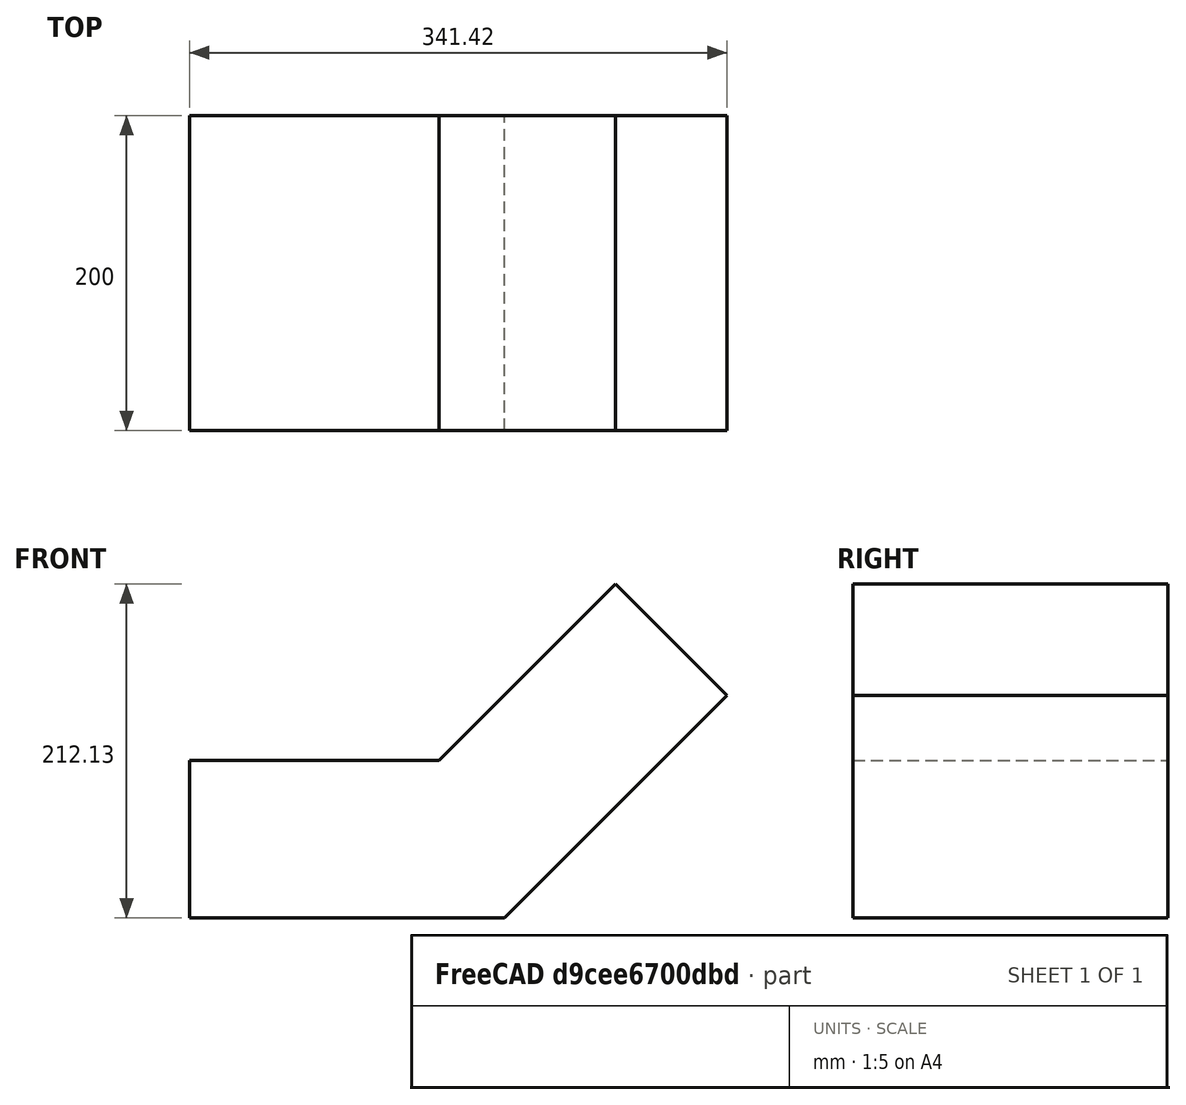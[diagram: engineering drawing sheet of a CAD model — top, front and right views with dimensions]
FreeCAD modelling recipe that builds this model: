
FCSTD DOCUMENT  (FreeCAD 0.16R6706 (Git))
Label: 45 degree part
License: All rights reserved
LicenseURL: http://en.wikipedia.org/wiki/All_rights_reserved
objects: Sketcher::SketchObject×1, PartDesign::Pad×1, Drawing::FeatureViewPart×1, Drawing::FeaturePage×1
note: 3 computed .brp shape members not serialized (recipe doc carries the construction recipe); baked Part::Feature solids carry a one-line shape summary decoded from their .brp

FEATURE [Sketcher::SketchObject] Sketch
  Placement = pos=(0,0,0) rot=(1,0,0;1.5708rad)
  sketch-geometry (6):
    g0: LineSegment StartX=-200 StartY=100 StartZ=0 EndX=-200 EndY=0 EndZ=0
    g1: LineSegment StartX=-200 StartY=0 StartZ=0 EndX=0 EndY=0 EndZ=0
    g2: LineSegment StartX=0 StartY=0 StartZ=0 EndX=141.421 EndY=141.421 EndZ=0
    g3: LineSegment StartX=141.421 StartY=141.421 StartZ=0 EndX=70.7107 EndY=212.132 EndZ=0
    g4: LineSegment StartX=70.7107 StartY=212.132 StartZ=0 EndX=-41.4214 EndY=100 EndZ=0
    g5: LineSegment StartX=-41.4214 StartY=100 StartZ=0 EndX=-200 EndY=100 EndZ=0
  constraints (17):
    c: PointOnObject(g0,g-1)
    c: Vertical(g0)
    c: Coincident(g0,g1)
    c: Coincident(g1,g-1)
    c: Coincident(g1,g2)
    c: Coincident(g2,g3)
    c: Coincident(g3,g4)
    c: Perpendicular(g2,g3)
    c: Parallel(g4,g2)
    c: Angle(g-1,g2) = 0.785398
    c: DistanceY(g0,g0) = 100
    c: Equal(g3,g0)
    c: Coincident(g5,g4)
    c: Coincident(g5,g0)
    c: Horizontal(g5)
    c: DistanceX(g1,g1) = 200
    c: Distance(g2) = 200
FEATURE [PartDesign::Pad] Pad
  Length = 200
  Length2 = 100
  Placement = pos=(0,0,0) rot=(1,0,0;1.5708rad)
  Reversed = true
  Sketch = -> Sketch
  Type = 0
FEATURE [Drawing::FeatureViewPart] View
  Direction = (1,-1,1)
  HiddenWidth = 0.15
  LineWidth = 0.35
  Rotation = 60
  Scale = 0.2
  ShowHiddenLines = false
  ShowSmoothLines = false
  Source = -> Pad
  Tolerance = 0.05
  ViewResult = <g id="View"\n   transform="rotate(60,95,172.995) translate(95,172.995) scale(0.2,0.2)"\n  >\n<g   stroke="rgb(0, 0, 0)"\n   stroke-width="1.75"\n   stroke-linecap="butt"\n   stroke-linejoin="miter"\n   fill="none"\n   transform="scale(1,-1)"\n  >\n<path id= "1" d=" M -212.132 -40.8248 L -212.132 122.474 " />\n<path id= "2" d=" M -212.132 -40.8248 L -141.421 -81.6497 " />\n<path id= "3" d=" M -141.421 -81.6497 L 2.84217e-14 1.42109e-14 " />\n<path id= "4" d=" M 0 115.47 L 6.28037e-14 278.769 " />\n<path id= "5" d=" M 0 0 L 0 115.47 " />\n<path id= "6" d=" M -100 115.47 L -100 278.769 " />\n<path id= "7" d=" M 0 115.47 L -100 115.47 " />\n<path id= "8" d=" M 7.10543e-14 278.769 L -100 278.769 " />\n<path id= "9" d=" M -100 23.9146 L -100 115.47 " />\n<path id= "10" d=" M -100 115.47 L -100 23.9146 " />\n<path id= "11" d=" M -100 23.9146 L -212.132 -40.8248 " />\n<path id= "12" d=" M -100 187.214 L -212.132 122.474 " />\n</g>\n</g>
  Visible = true
  X = 95
  Y = 172.995
FEATURE [Drawing::FeaturePage] Page
  Group = -> [View]
